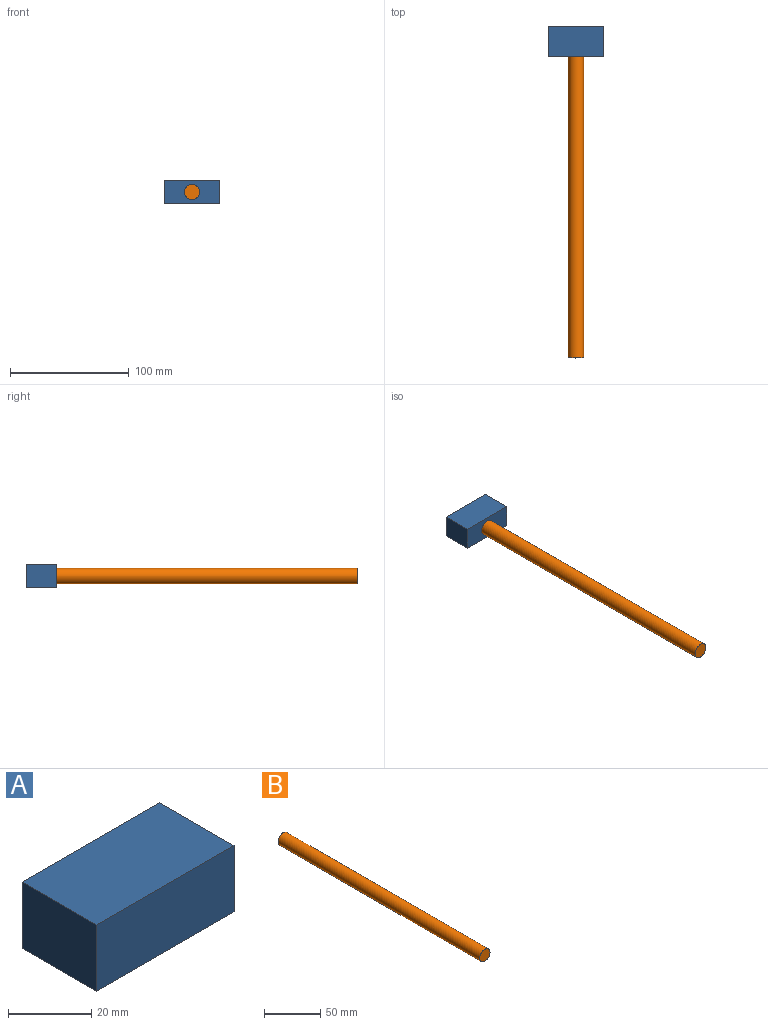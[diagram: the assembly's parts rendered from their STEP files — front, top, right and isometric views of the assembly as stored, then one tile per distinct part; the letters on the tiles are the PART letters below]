
ASSEMBLY  parts=2 mates=1
PART A: 6 faces, bbox 46.8x25.4x19.5 mm
  f0: plane 25.4x19.54mm, normal (-1,0,0), area 496.4mm2, adj f1,f3,f4,f5
  f1: plane 46.83x25.4mm, normal (0,0,-1), area 1189.4mm2, adj f0,f2,f4,f5
  f2: plane 25.4x19.54mm, normal (1,0,0), area 496.4mm2, adj f1,f3,f4,f5
  f3: plane 46.83x25.4mm, normal (0,0,1), area 1189.4mm2, adj f0,f2,f4,f5
  f4: plane 46.83x19.54mm, normal (0,-1,0), area 915.1mm2, adj f0,f1,f2,f3
  f5: plane 46.83x19.54mm, normal (0,1,0), area 915.1mm2, adj f0,f1,f2,f3
PART B: 3 faces, bbox 12.9x254x12.9 mm
  f0: cylinder r=6.46mm len=254mm, axis (0,1,0), area 10314.4mm2, adj f1,f2
  f1: plane 12.93x12.93mm, normal (0,-1,0), area 131.2mm2, adj f0
  f2: plane 12.93x12.93mm, normal (0,1,0), area 131.2mm2, adj f0
PLACE A t=(-82.47,125.96,-48.62)mm
PLACE B t=(-41.17,100.56,-4.01)mm
MATE planar A.f4 <-> B.f0  axis (0,-1,0) through (-41.17,100.56,-4.01)mm
